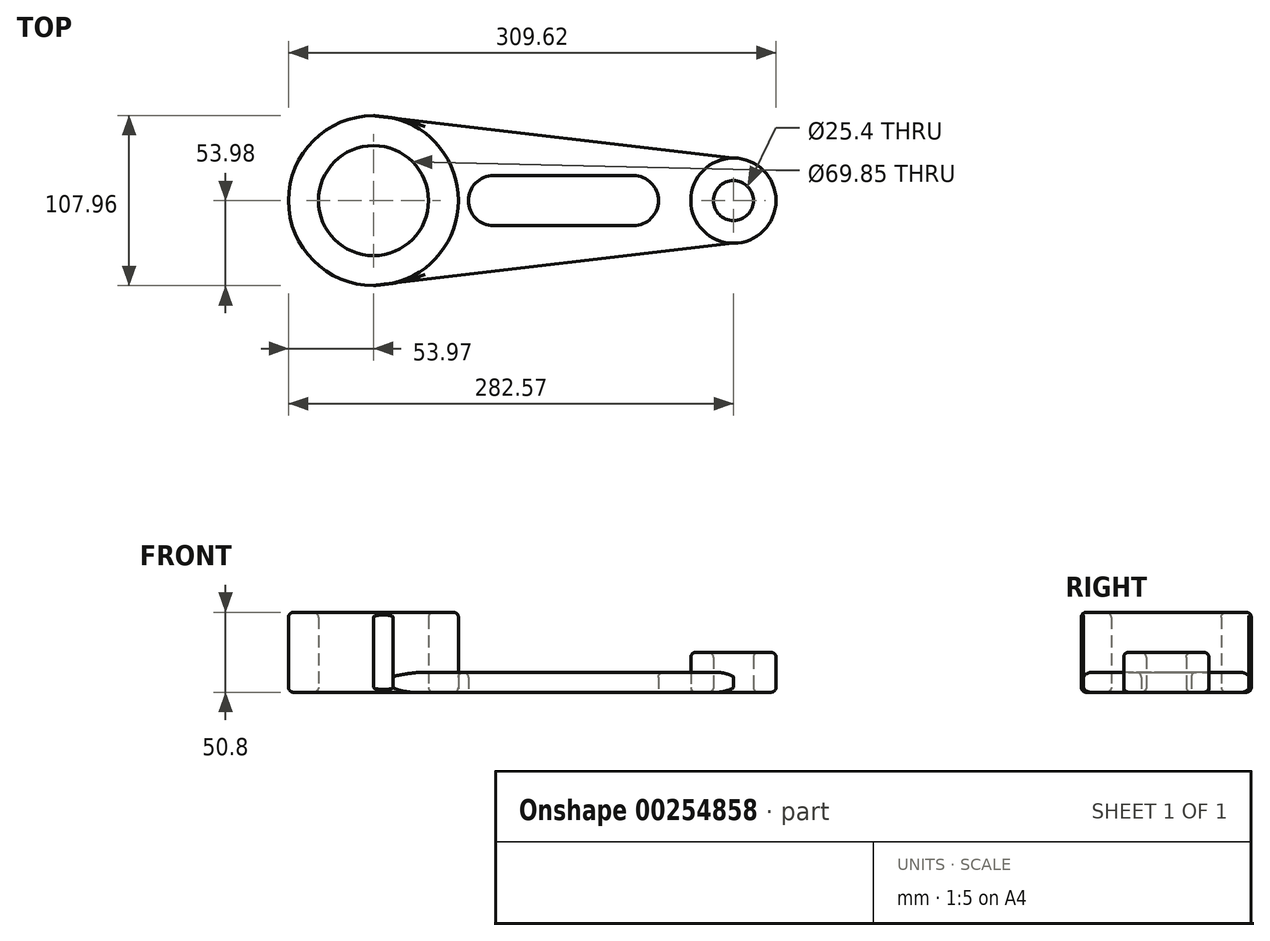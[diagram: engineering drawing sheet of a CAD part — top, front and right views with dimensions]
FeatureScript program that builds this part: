
annotation { "Feature Type Name" : "Feature", "Feature Type Description" : "" }
export const myFeature = defineFeature(function(context is Context, id is Id, definition is map)
    precondition{}
    {
        {
            var Q0;
            Q0=qCreatedBy(makeId("Top.planeOp"),FACE);
            var sketch = newSketch(context, id + "F0", { "sketchPlane" : qUnion([Q0])});
            skCircle(sketch, "E0", {"center": v(108.83, 0) * mm, "radius": 12.7 * mm});
            skCircle(sketch, "E1", {"center": v(108.83, 0) * mm, "radius": 27.05 * mm});
            skArc(sketch, "E2", {"start": v(45.33, -15.88) * mm, "mid": v(61.2, 0) * mm, "end": v(45.33, 15.88) * mm});
            skArc(sketch, "E3", {"start": v(-43.57, 15.88) * mm, "mid": v(-59.44, 0) * mm, "end": v(-43.57, -15.88) * mm});
            skCircle(sketch, "E4", {"center": v(-119.77, 0) * mm, "radius": 34.93 * mm});
            skCircle(sketch, "E5", {"center": v(-119.77, 0) * mm, "radius": 53.98 * mm});
            skLineSegment(sketch, "E6", {"start": v(108.83, 27.05) * mm, "end": v(-119.77, 53.97) * mm});
            skLineSegment(sketch, "E7", {"start": v(108.83, -27.05) * mm, "end": v(-119.77, -53.97) * mm});
            skLineSegment(sketch, "E8", {"start": v(-43.57, 15.88) * mm, "end": v(45.33, 15.88) * mm});
            skLineSegment(sketch, "E9", {"start": v(45.33, -15.88) * mm, "end": v(-43.57, -15.88) * mm});
            skSolve(sketch);
        }
        {
            var Q0;
            Q0=makeQuery(id+"F0.imprint","IMPRINT",FACE,{"disambiguationData":[TD([[makeQuery(id+"F0.imprint","IMPRINT",EDGE,{"derivedFrom":sQuery(id+"F0.wireOp",EDGE,"E4")}),-1.0]])]});
            extrude(context, id + "F1", {"entities" : qUnion([Q0]), "depth" : 50.8 * mm});
        }
        {
            var Q0;
            Q0=makeQuery(id+"F0.imprint","IMPRINT",FACE,{"disambiguationData":[TD([[makeQuery(id+"F0.imprint","IMPRINT",EDGE,{"derivedFrom":sQuery(id+"F0.wireOp",EDGE,"E0")}),-1.0]])]});
            extrude(context, id + "F2", {"entities" : qUnion([Q0]), "depth" : 25.4 * mm});
        }
        {
            var Q0;
            Q0=makeQuery(id+"F0.imprint","IMPRINT",FACE,{"disambiguationData":[TD([[makeQuery(id+"F0.imprint","IMPRINT",EDGE,{"derivedFrom":sQuery(id+"F0.wireOp",EDGE,"E2")}),-1.0]])]});
            extrude(context, id + "F3", {"entities" : qUnion([Q0]), "depth" : 12.7 * mm});
        }
        {
            var Q0;
            {var subQ0=sQuery(id+"F0.wireOp",EDGE,"E5");Q0=makeQuery(id+"F1.opExtrude","CAP_EDGE",EDGE,{"disambiguationData":[OSD([subQ0]),TDD([makeQuery(id+"F0.imprint","IMPRINT",EDGE,{"disambiguationData":[TD([[makeQuery(id+"F0.imprint","INTERSECT",VERTEX,{"disambiguationData":[OD(1.0)],"derivedFrom":[subQ0,sQuery(id+"F0.wireOp",EDGE,"E6")]}),1.0]])],"derivedFrom":subQ0})])],"isStart":false});}
            var Q1;
            {var subQ0=sQuery(id+"F0.wireOp",EDGE,"E5");Q1=makeQuery(id+"F1.opExtrude","CAP_EDGE",EDGE,{"disambiguationData":[OSD([subQ0]),TDD([makeQuery(id+"F0.imprint","IMPRINT",EDGE,{"disambiguationData":[TD([[makeQuery(id+"F0.imprint","INTERSECT",VERTEX,{"disambiguationData":[OD(0.0)],"derivedFrom":[subQ0,sQuery(id+"F0.wireOp",EDGE,"E6")]}),-1.0]])],"derivedFrom":subQ0})])],"isStart":true});}
            var Q2;
            Q2=makeQuery(id+"F3.opExtrude","CAP_EDGE",EDGE,{"disambiguationData":[OSD([sQuery(id+"F0.wireOp",EDGE,"E5")])],"isStart":false});
            var Q3;
            Q3=makeQuery(id+"F3.opExtrude","CAP_EDGE",EDGE,{"disambiguationData":[OSD([sQuery(id+"F0.wireOp",EDGE,"E7")])],"isStart":false});
            var Q4;
            Q4=makeQuery(id+"F3.opExtrude","CAP_EDGE",EDGE,{"disambiguationData":[OSD([sQuery(id+"F0.wireOp",EDGE,"E7")])],"isStart":true});
            var Q5;
            Q5=makeQuery(id+"F3.opExtrude","CAP_EDGE",EDGE,{"disambiguationData":[OSD([sQuery(id+"F0.wireOp",EDGE,"E6")])],"isStart":false});
            var Q6;
            Q6=makeQuery(id+"F3.opExtrude","CAP_EDGE",EDGE,{"disambiguationData":[OSD([sQuery(id+"F0.wireOp",EDGE,"E6")])],"isStart":true});
            var Q7;
            Q7=makeQuery(id+"F2.opExtrude","CAP_EDGE",EDGE,{"disambiguationData":[OSD([sQuery(id+"F0.wireOp",EDGE,"E1")])],"isStart":false});
            var Q8;
            Q8=makeQuery(id+"F2.opExtrude","CAP_EDGE",EDGE,{"disambiguationData":[OSD([sQuery(id+"F0.wireOp",EDGE,"E1")])],"isStart":true});
            fillet(context, id + "F4", {"entities" : qUnion([Q0, Q1, Q2, Q3, Q4, Q5, Q6, Q7, Q8]), "radius" : 3.17 * mm, "tangentPropagation" : true, "allowEdgeOverflow" : false});
        }
        {
            var Q0;
            Q0=makeQuery(id+"F3.opExtrude","CAP_EDGE",EDGE,{"disambiguationData":[OSD([sQuery(id+"F0.wireOp",EDGE,"E8")])],"isStart":false});
            var Q1;
            Q1=makeQuery(id+"F3.opExtrude","CAP_EDGE",EDGE,{"disambiguationData":[OSD([sQuery(id+"F0.wireOp",EDGE,"E9")])],"isStart":false});
            var Q2;
            Q2=makeQuery(id+"F3.opExtrude","CAP_EDGE",EDGE,{"disambiguationData":[OSD([sQuery(id+"F0.wireOp",EDGE,"E3")])],"isStart":false});
            var Q3;
            Q3=makeQuery(id+"F3.opExtrude","CAP_EDGE",EDGE,{"disambiguationData":[OSD([sQuery(id+"F0.wireOp",EDGE,"E2")])],"isStart":false});
            fillet(context, id + "F5", {"entities" : qUnion([Q0, Q1, Q2, Q3]), "radius" : 3.17 * mm, "tangentPropagation" : true, "allowEdgeOverflow" : false});
        }
        {
            var Q0;
            Q0=makeQuery(id+"F1.opExtrude","CAP_EDGE",EDGE,{"disambiguationData":[OSD([sQuery(id+"F0.wireOp",EDGE,"E4")])],"isStart":false});
            var Q1;
            Q1=makeQuery(id+"F2.opExtrude","CAP_EDGE",EDGE,{"disambiguationData":[OSD([sQuery(id+"F0.wireOp",EDGE,"E0")])],"isStart":false});
            var Q2;
            Q2=makeQuery(id+"F1.opExtrude","CAP_EDGE",EDGE,{"disambiguationData":[OSD([sQuery(id+"F0.wireOp",EDGE,"E4")])],"isStart":true});
            var Q3;
            Q3=makeQuery(id+"F2.opExtrude","CAP_EDGE",EDGE,{"disambiguationData":[OSD([sQuery(id+"F0.wireOp",EDGE,"E0")])],"isStart":true});
            fillet(context, id + "F6", {"entities" : qUnion([Q0, Q1, Q2, Q3]), "radius" : 3.17 * mm, "tangentPropagation" : true, "allowEdgeOverflow" : false});
        }
    });
